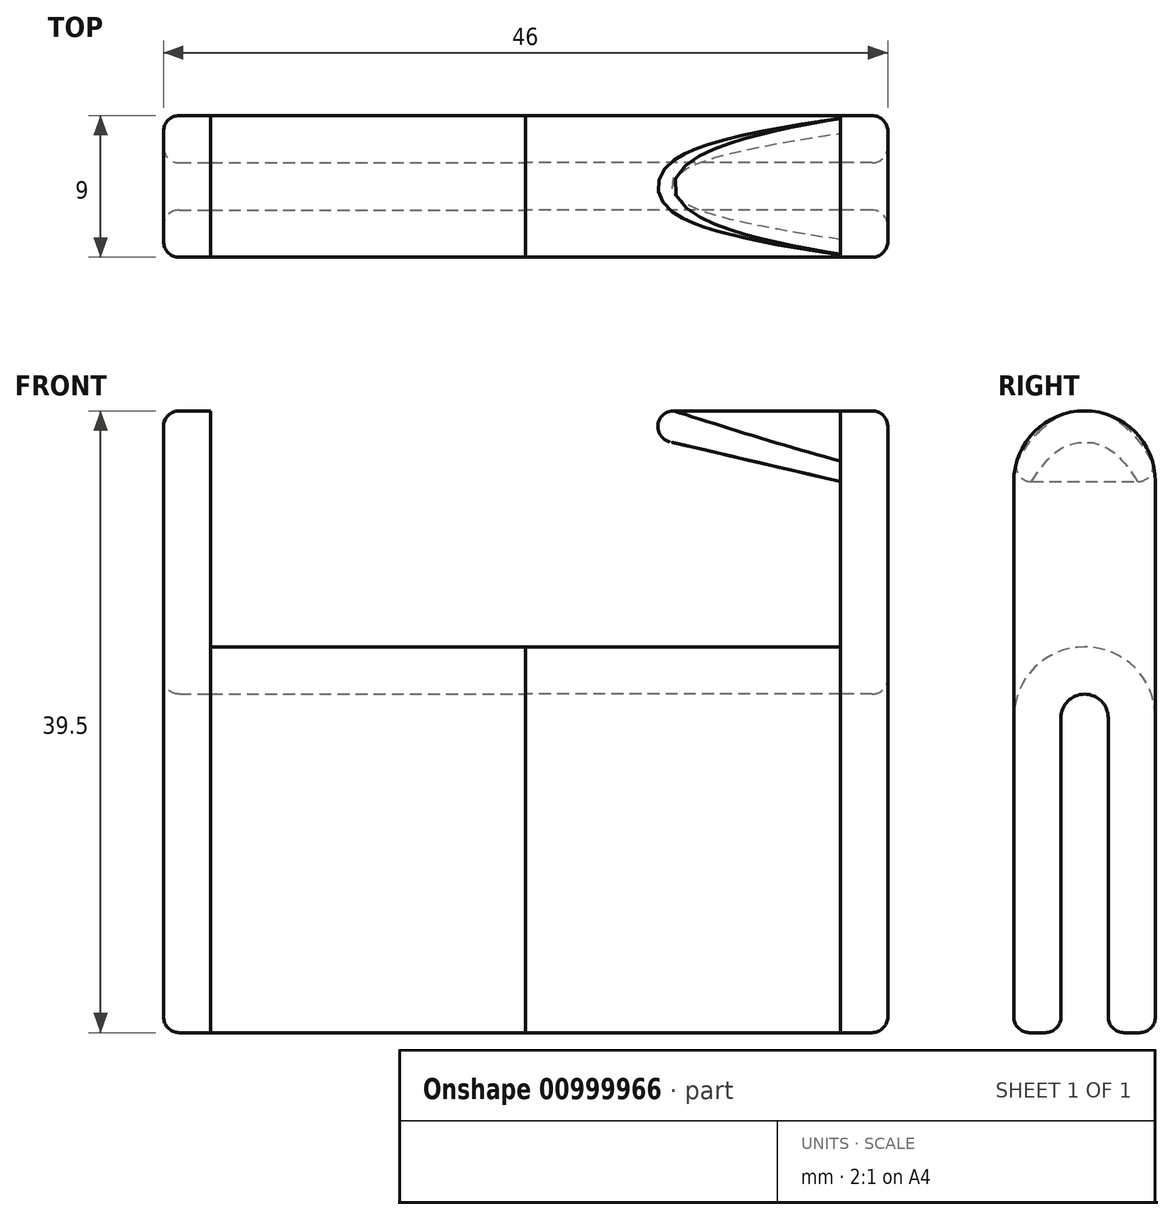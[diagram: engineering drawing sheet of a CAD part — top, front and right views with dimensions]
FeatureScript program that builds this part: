
annotation { "Feature Type Name" : "Feature", "Feature Type Description" : "" }
export const myFeature = defineFeature(function(context is Context, id is Id, definition is map)
    precondition{}
    {
        {
            var Q0;
            Q0=qCreatedBy(makeId("Right.planeOp"),FACE);
            var sketch = newSketch(context, id + "F0", { "sketchPlane" : qUnion([Q0])});
            skArc(sketch, "E0", {"start": v(1.5, 0) * mm, "mid": v(0, 1.5) * mm, "end": v(-1.5, 0) * mm});
            skLineSegment(sketch, "E1.left", {"start": v(-1.5, 0) * mm, "end": v(-1.5, -20) * mm});
            skLineSegment(sketch, "E1.right", {"start": v(1.5, 0) * mm, "end": v(1.5, -20) * mm});
            skLineSegment(sketch, "E2.0", {"start": v(-4.5, 0) * mm, "end": v(-4.5, -20) * mm});
            skArc(sketch, "E2.1", {"start": v(4.5, 0) * mm, "mid": v(0, 4.5) * mm, "end": v(-4.5, 0) * mm});
            skLineSegment(sketch, "E2.2", {"start": v(4.5, 0) * mm, "end": v(4.5, -20) * mm});
            skLineSegment(sketch, "E3", {"start": v(-4.5, -20) * mm, "end": v(-1.5, -20) * mm});
            skLineSegment(sketch, "E4", {"start": v(1.5, -20) * mm, "end": v(4.5, -20) * mm});
            skArc(sketch, "E5.1", {"start": v(4.5, 15) * mm, "mid": v(0, 19.5) * mm, "end": v(-4.5, 15) * mm});
            skLineSegment(sketch, "E6", {"start": v(-4.5, 0) * mm, "end": v(-4.5, 15) * mm});
            skLineSegment(sketch, "E7", {"start": v(4.5, 0) * mm, "end": v(4.5, 15) * mm});
            skSolve(sketch);
        }
        {
            var Q0;
            Q0=makeQuery(id+"F0.imprint","IMPRINT",FACE,{"disambiguationData":[TD([[makeQuery(id+"F0.imprint","IMPRINT",EDGE,{"derivedFrom":sQuery(id+"F0.wireOp",EDGE,"E0")}),-1.0]])]});
            extrude(context, id + "F1", {"entities" : qUnion([Q0]), "depth" : 20 * mm, "offsetDistance" : 25 * mm});
        }
        {
            var Q0;
            Q0=makeQuery(id+"F0.imprint","IMPRINT",FACE,{"disambiguationData":[TD([[makeQuery(id+"F0.imprint","IMPRINT",EDGE,{"derivedFrom":sQuery(id+"F0.wireOp",EDGE,"E0")}),-1.0]])]});
            var Q1;
            Q1=makeQuery(id+"F0.imprint","IMPRINT",FACE,{"disambiguationData":[TD([[makeQuery(id+"F0.imprint","IMPRINT",EDGE,{"derivedFrom":sQuery(id+"F0.wireOp",EDGE,"E2.1")}),-1.0]])]});
            extrude(context, id + "F2", {"entities" : qUnion([Q0, Q1]), "depth" : 3 * mm, "offsetDistance" : 25 * mm});
        }
        {
            var Q0;
            Q0=makeQuery(id+"F2.opExtrude","SWEPT_BODY",BODY,{"disambiguationData":[OSD([sQuery(id+"F0.wireOp",EDGE,"E0"),sQuery(id+"F0.wireOp",EDGE,"E1.left"),sQuery(id+"F0.wireOp",EDGE,"E1.right"),sQuery(id+"F0.wireOp",EDGE,"E3"),sQuery(id+"F0.wireOp",EDGE,"E4"),sQuery(id+"F0.wireOp",EDGE,"1357690b-98cf-45ee-a855-5e802a0c79e5.0"),sQuery(id+"F0.wireOp",EDGE,"1357690b-98cf-45ee-a855-5e802a0c79e5.1"),sQuery(id+"F0.wireOp",EDGE,"1357690b-98cf-45ee-a855-5e802a0c79e5.2"),sQuery(id+"F0.wireOp",EDGE,"wXfNaB6y-MYRl-YLl9-LbBf-jZJ8hGzQo1M2"),sQuery(id+"F0.wireOp",EDGE,"lHjYiNPH-YhLH-P8Ia-Ohss-T36oArsf0li4")])]});
            var Q1;
            Q1=makeQuery(id+"F1.opExtrude","SWEPT_EDGE",EDGE,{"disambiguationData":[OSD([sQuery(id+"F0.wireOp",EDGE,"E2.2"),sQuery(id+"F0.wireOp",EDGE,"E4"),sQuery(id+"F0.wireOp",EDGE,"lHjYiNPH-YhLH-P8Ia-Ohss-T36oArsf0li4")])]});
            transform(context, id + "F3", {"entities" : qUnion([Q0]), "transformType" : TransformType.TRANSLATION_ENTITY, "oppositeDirectionEntity" : true, "transformLine" : qUnion([Q1]), "makeCopy" : false});
        }
        {
            var Q0;
            Q0=makeQuery(id+"F2.opExtrude","CAP_EDGE",EDGE,{"disambiguationData":[OSD([sQuery(id+"F0.wireOp",EDGE,"E1.right")])],"isStart":false});
            var Q1;
            Q1=makeQuery(id+"F2.opExtrude","CAP_EDGE",EDGE,{"disambiguationData":[OSD([sQuery(id+"F0.wireOp",EDGE,"1357690b-98cf-45ee-a855-5e802a0c79e5.1")])],"isStart":false});
            var Q2;
            Q2=makeQuery(id+"F2.opExtrude","CAP_EDGE",EDGE,{"disambiguationData":[OSD([sQuery(id+"F0.wireOp",EDGE,"1357690b-98cf-45ee-a855-5e802a0c79e5.0")])],"isStart":true});
            fillet(context, id + "F4", {"entities" : qUnion([Q0, Q1, Q2]), "radius" : 1 * mm, "tangentPropagation" : true, "allowEdgeOverflow" : false});
        }
        {
            var Q0;
            Q0=makeQuery(id+"F1.opExtrude","SWEPT_EDGE",EDGE,{"disambiguationData":[OSD([sQuery(id+"F0.wireOp",EDGE,"E2.0"),sQuery(id+"F0.wireOp",EDGE,"E3"),sQuery(id+"F0.wireOp",EDGE,"wXfNaB6y-MYRl-YLl9-LbBf-jZJ8hGzQo1M2")])]});
            var Q1;
            Q1=makeQuery(id+"F1.opExtrude","SWEPT_EDGE",EDGE,{"disambiguationData":[OSD([sQuery(id+"F0.wireOp",EDGE,"E1.left"),sQuery(id+"F0.wireOp",EDGE,"E3")])]});
            var Q2;
            Q2=makeQuery(id+"F1.opExtrude","SWEPT_EDGE",EDGE,{"disambiguationData":[OSD([sQuery(id+"F0.wireOp",EDGE,"E1.right"),sQuery(id+"F0.wireOp",EDGE,"E4")])]});
            var Q3;
            Q3=makeQuery(id+"F1.opExtrude","SWEPT_EDGE",EDGE,{"disambiguationData":[OSD([sQuery(id+"F0.wireOp",EDGE,"E2.2"),sQuery(id+"F0.wireOp",EDGE,"E4"),sQuery(id+"F0.wireOp",EDGE,"lHjYiNPH-YhLH-P8Ia-Ohss-T36oArsf0li4")])]});
            var Q4;
            Q4=makeQuery(id+"F2.opExtrude","SWEPT_EDGE",EDGE,{"disambiguationData":[OSD([sQuery(id+"F0.wireOp",EDGE,"E2.2"),sQuery(id+"F0.wireOp",EDGE,"E4")])]});
            var Q5;
            Q5=makeQuery(id+"F2.opExtrude","SWEPT_EDGE",EDGE,{"disambiguationData":[OSD([sQuery(id+"F0.wireOp",EDGE,"E2.0"),sQuery(id+"F0.wireOp",EDGE,"E3")])]});
            var Q6;
            Q6=makeQuery(id+"F2.opExtrude","CAP_EDGE",EDGE,{"disambiguationData":[OSD([sQuery(id+"F0.wireOp",EDGE,"E4")])],"isStart":false});
            var Q7;
            Q7=makeQuery(id+"F2.opExtrude","CAP_EDGE",EDGE,{"disambiguationData":[OSD([sQuery(id+"F0.wireOp",EDGE,"E3")])],"isStart":false});
            var Q8;
            Q8=makeQuery(id+"F2.opExtrude","CAP_EDGE",EDGE,{"disambiguationData":[OSD([sQuery(id+"F0.wireOp",EDGE,"E2.2"),sQuery(id+"F0.wireOp",EDGE,"E7")])],"isStart":false});
            var Q9;
            Q9=makeQuery(id+"F2.opExtrude","CAP_EDGE",EDGE,{"disambiguationData":[OSD([sQuery(id+"F0.wireOp",EDGE,"E2.0"),sQuery(id+"F0.wireOp",EDGE,"E6")])],"isStart":false});
            fillet(context, id + "F5", {"entities" : qUnion([Q0, Q1, Q2, Q3, Q4, Q5, Q6, Q7, Q8, Q9]), "radius" : 1 * mm, "tangentPropagation" : true, "allowEdgeOverflow" : false});
        }
        {
            var Q0;
            Q0=makeQuery(id+"F2.opExtrude","CAP_FACE",FACE,{"disambiguationData":[OSD([sQuery(id+"F0.wireOp",EDGE,"E0"),sQuery(id+"F0.wireOp",EDGE,"E1.left"),sQuery(id+"F0.wireOp",EDGE,"E1.right"),sQuery(id+"F0.wireOp",EDGE,"E2.0"),sQuery(id+"F0.wireOp",EDGE,"E2.2"),sQuery(id+"F0.wireOp",EDGE,"E3"),sQuery(id+"F0.wireOp",EDGE,"E4"),sQuery(id+"F0.wireOp",EDGE,"E5.1"),sQuery(id+"F0.wireOp",EDGE,"E6"),sQuery(id+"F0.wireOp",EDGE,"E7")])],"isStart":true});
            cPlane(context, id + "F6", {"entities" : qUnion([Q0]), "cplaneType" : CPlaneType.OFFSET, "offset" : 0 * mm, "width" : 150 * mm, "height" : 150 * mm});
        }
        {
            var Q0;
            Q0=qCreatedBy(id+"F6.planeOp",FACE);
            var sketch = newSketch(context, id + "F7", { "sketchPlane" : qUnion([Q0])});
            skArc(sketch, "E8", {"start": v(4.5, 15) * mm, "mid": v(0, 19.5) * mm, "end": v(-4.5, 15) * mm});
            skLineSegment(sketch, "E9", {"start": v(4.5, 15) * mm, "end": v(-4.5, 15) * mm});
            skSolve(sketch);
        }
        {
            var Q0;
            Q0=qCreatedBy(id+"F6.planeOp",FACE);
            cPlane(context, id + "F8", {"entities" : qUnion([Q0]), "cplaneType" : CPlaneType.OFFSET, "offset" : 15 * mm, "width" : 150 * mm, "height" : 150 * mm});
        }
        {
            var Q0;
            Q0=qCreatedBy(id+"F8.planeOp",FACE);
            var sketch = newSketch(context, id + "F9", { "sketchPlane" : qUnion([Q0])});
            skArc(sketch, "E10", {"start": v(2.83, 18.5) * mm, "mid": v(0, 19.5) * mm, "end": v(-2.83, 18.5) * mm});
            skLineSegment(sketch, "E11", {"start": v(2.83, 18.5) * mm, "end": v(-2.83, 18.5) * mm});
            skSolve(sketch);
        }
        {
            var Q0;
            Q0=makeQuery(id+"F7.imprint","IMPRINT",FACE,{"disambiguationData":[TD([[makeQuery(id+"F7.imprint","IMPRINT",EDGE,{"derivedFrom":sQuery(id+"F7.wireOp",EDGE,"E8")}),1.0]])]});
            var Q1;
            Q1 = qSketchRegion(id + "F9", true);
            loft(context, id + "F10", {"sheetProfilesArray" : [{ "sheetProfileEntities" : qUnion([Q0]) }, { "sheetProfileEntities" : qUnion([Q1]) }]});
        }
        {
            var Q0;
            {var subQ0=sQuery(id+"F9.wireOp",EDGE,"E11");var subQ1=sQuery(id+"F9.wireOp",EDGE,"E10");var subQ2=sQuery(id+"F7.wireOp",EDGE,"E9");var subQ3=sQuery(id+"F7.wireOp",EDGE,"E8");Q0=makeQuery(id+"F10.opLoft","SWEPT_EDGE",EDGE,{"disambiguationData":[OSD([subQ3,subQ2,subQ1,subQ0]),TDD([makeQuery(id+"F7.imprint","INTERSECT",VERTEX,{"disambiguationData":[OD(0.0)],"derivedFrom":[subQ3,subQ2]}),makeQuery(id+"F9.imprint","INTERSECT",VERTEX,{"disambiguationData":[OD(0.0)],"derivedFrom":[subQ1,subQ0]})])]});}
            var Q1;
            {var subQ0=sQuery(id+"F9.wireOp",EDGE,"E11");var subQ1=sQuery(id+"F9.wireOp",EDGE,"E10");var subQ2=sQuery(id+"F7.wireOp",EDGE,"E9");var subQ3=sQuery(id+"F7.wireOp",EDGE,"E8");Q1=makeQuery(id+"F10.opLoft","SWEPT_EDGE",EDGE,{"disambiguationData":[OSD([subQ3,subQ2,subQ1,subQ0]),TDD([makeQuery(id+"F7.imprint","INTERSECT",VERTEX,{"disambiguationData":[OD(1.0)],"derivedFrom":[subQ3,subQ2]}),makeQuery(id+"F9.imprint","INTERSECT",VERTEX,{"disambiguationData":[OD(1.0)],"derivedFrom":[subQ1,subQ0]})])]});}
            var Q2;
            {var subQ0=sQuery(id+"F9.wireOp",EDGE,"E10");var subQ1=sQuery(id+"F9.wireOp",EDGE,"E11");Q2=makeQuery(id+"F10.opLoft","MID_CAP_EDGE",EDGE,{"disambiguationData":[OSD([subQ0,subQ1]),TDD([makeQuery(id+"F9.imprint","INTERSECT",VERTEX,{"disambiguationData":[OD(0.0)],"derivedFrom":[subQ0,subQ1]}),makeQuery(id+"F9.imprint","INTERSECT",VERTEX,{"disambiguationData":[OD(1.0)],"derivedFrom":[subQ0,subQ1]}),makeQuery(id+"F9.imprint","IMPRINT",EDGE,{"derivedFrom":subQ0})])],"capPos":1.0});}
            fillet(context, id + "F11", {"entities" : qUnion([Q0, Q1, Q2]), "radius" : 1 * mm, "tangentPropagation" : true, "allowEdgeOverflow" : false});
        }
        {
            var Q0;
            Q0=makeQuery(id+"F1.opExtrude","SWEPT_BODY",BODY,{"disambiguationData":[OSD([sQuery(id+"F0.wireOp",EDGE,"E0"),sQuery(id+"F0.wireOp",EDGE,"E1.left"),sQuery(id+"F0.wireOp",EDGE,"E1.right"),sQuery(id+"F0.wireOp",EDGE,"E2.0"),sQuery(id+"F0.wireOp",EDGE,"E2.1"),sQuery(id+"F0.wireOp",EDGE,"E2.2"),sQuery(id+"F0.wireOp",EDGE,"E3"),sQuery(id+"F0.wireOp",EDGE,"E4")])]});
            var Q1;
            Q1=makeQuery(id+"F2.opExtrude","SWEPT_BODY",BODY,{"disambiguationData":[OSD([sQuery(id+"F0.wireOp",EDGE,"E0"),sQuery(id+"F0.wireOp",EDGE,"E1.left"),sQuery(id+"F0.wireOp",EDGE,"E1.right"),sQuery(id+"F0.wireOp",EDGE,"E3"),sQuery(id+"F0.wireOp",EDGE,"E4"),sQuery(id+"F0.wireOp",EDGE,"1357690b-98cf-45ee-a855-5e802a0c79e5.0"),sQuery(id+"F0.wireOp",EDGE,"1357690b-98cf-45ee-a855-5e802a0c79e5.1"),sQuery(id+"F0.wireOp",EDGE,"1357690b-98cf-45ee-a855-5e802a0c79e5.2"),sQuery(id+"F0.wireOp",EDGE,"wXfNaB6y-MYRl-YLl9-LbBf-jZJ8hGzQo1M2"),sQuery(id+"F0.wireOp",EDGE,"lHjYiNPH-YhLH-P8Ia-Ohss-T36oArsf0li4")])]});
            var Q2;
            Q2=qCreatedBy(makeId("Right.planeOp"),FACE);
            mirror(context, id + "F12", {"entities" : qUnion([Q0, Q1]), "mirrorPlane" : qUnion([Q2])});
        }
    });
